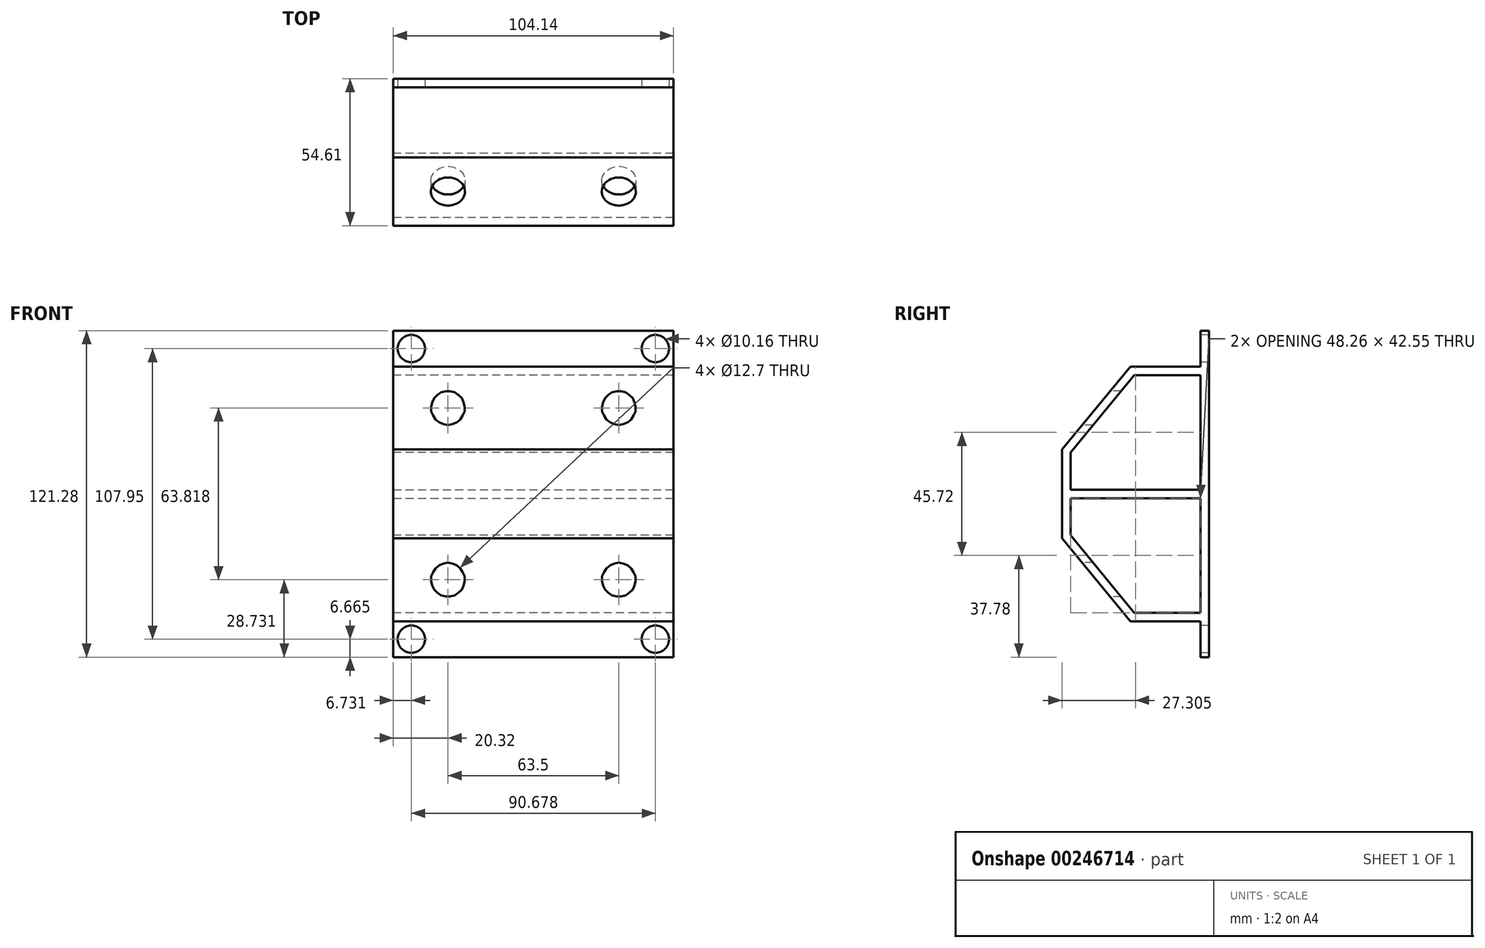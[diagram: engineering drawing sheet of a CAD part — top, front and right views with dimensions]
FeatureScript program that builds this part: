
annotation { "Feature Type Name" : "Feature", "Feature Type Description" : "" }
export const myFeature = defineFeature(function(context is Context, id is Id, definition is map)
    precondition{}
    {
        {
            var Q0;
            Q0=qCreatedBy(makeId("Right.planeOp"),FACE);
            var sketch = newSketch(context, id + "F0", { "sketchPlane" : qUnion([Q0])});
            skLineSegment(sketch, "E0", {"start": v(0, 0) * mm, "end": v(57.67, 0) * mm, "construction": true});
            skLineSegment(sketch, "E1", {"start": v(29.21, 47.3) * mm, "end": v(0, 47.3) * mm});
            skLineSegment(sketch, "E2", {"start": v(0, 47.3) * mm, "end": v(-25.4, 16.51) * mm});
            skLineSegment(sketch, "E3", {"start": v(-25.4, 16.51) * mm, "end": v(-25.4, 0) * mm});
            skLineSegment(sketch, "E4", {"start": v(0, 0) * mm, "end": v(0, 100.35) * mm, "construction": true});
            skLineSegment(sketch, "E5", {"start": v(29.21, 47.3) * mm, "end": v(29.21, 0) * mm});
            skLineSegment(sketch, "E6.MirrorCS", {"start": v(29.21, -47.3) * mm, "end": v(29.21, 0) * mm});
            skLineSegment(sketch, "E7.MirrorCS", {"start": v(0, -47.3) * mm, "end": v(-25.4, -16.51) * mm});
            skLineSegment(sketch, "E8.MirrorCS", {"start": v(-25.4, -16.51) * mm, "end": v(-25.4, 0) * mm});
            skLineSegment(sketch, "E9.MirrorCS", {"start": v(29.21, -47.3) * mm, "end": v(0, -47.3) * mm});
            skLineSegment(sketch, "E10", {"start": v(-22.22, 3.17) * mm, "end": v(26.04, 3.17) * mm});
            skLineSegment(sketch, "E11.MirrorCS", {"start": v(-22.22, -3.17) * mm, "end": v(26.04, -3.17) * mm});
            skLineSegment(sketch, "E12.0", {"start": v(26.04, 44.13) * mm, "end": v(1.5, 44.13) * mm});
            skLineSegment(sketch, "E12.1", {"start": v(26.03, 44.13) * mm, "end": v(26.04, 0) * mm});
            skLineSegment(sketch, "E12.2", {"start": v(1.5, 44.13) * mm, "end": v(-22.22, 15.37) * mm});
            skLineSegment(sketch, "E12.3", {"start": v(26.04, -44.13) * mm, "end": v(26.03, 0) * mm});
            skLineSegment(sketch, "E12.4", {"start": v(-22.22, 15.37) * mm, "end": v(-22.22, 0) * mm});
            skLineSegment(sketch, "E12.5", {"start": v(-22.22, -15.37) * mm, "end": v(-22.22, 0) * mm});
            skLineSegment(sketch, "E12.6", {"start": v(1.5, -44.13) * mm, "end": v(-22.23, -15.37) * mm});
            skLineSegment(sketch, "E12.7", {"start": v(26.04, -44.13) * mm, "end": v(1.5, -44.13) * mm});
            skPoint(sketch, "E13.orphan", {"position": v(-25.4, 3.17) * mm});
            skPoint(sketch, "E14.orphan", {"position": v(-25.4, -3.17) * mm});
            skPoint(sketch, "E15.orphan", {"position": v(29.21, 3.18) * mm});
            skPoint(sketch, "E16.orphan", {"position": v(29.21, -3.18) * mm});
            skLineSegment(sketch, "E17", {"start": v(-22.22, 3.17) * mm, "end": v(-22.22, -3.17) * mm});
            skLineSegment(sketch, "E18", {"start": v(26.04, 3.18) * mm, "end": v(26.04, -3.18) * mm});
            skSolve(sketch);
        }
        {
            var Q0;
            Q0 = qSketchRegion(id + "F0", true);
            extrude(context, id + "F1", {"entities" : qUnion([Q0]), "depth" : 52.07 * mm, "hasSecondDirection" : true, "secondDirectionOppositeDirection" : true, "secondDirectionDepth" : 52.07 * mm});
        }
        {
            var Q0;
            Q0=makeQuery(id+"F1.opExtrude","CAP_FACE",FACE,{"disambiguationData":[OSD([sQuery(id+"F0.wireOp",EDGE,"E1"),sQuery(id+"F0.wireOp",EDGE,"E2"),sQuery(id+"F0.wireOp",EDGE,"E3"),sQuery(id+"F0.wireOp",EDGE,"E5"),sQuery(id+"F0.wireOp",EDGE,"E6.MirrorCS"),sQuery(id+"F0.wireOp",EDGE,"E7.MirrorCS"),sQuery(id+"F0.wireOp",EDGE,"E8.MirrorCS"),sQuery(id+"F0.wireOp",EDGE,"E9.MirrorCS"),sQuery(id+"F0.wireOp",EDGE,"E12.0"),sQuery(id+"F0.wireOp",EDGE,"E12.1"),sQuery(id+"F0.wireOp",EDGE,"E12.2"),sQuery(id+"F0.wireOp",EDGE,"E12.3"),sQuery(id+"F0.wireOp",EDGE,"E12.4"),sQuery(id+"F0.wireOp",EDGE,"E12.5"),sQuery(id+"F0.wireOp",EDGE,"E12.6"),sQuery(id+"F0.wireOp",EDGE,"E12.7"),sQuery(id+"F0.wireOp",EDGE,"E17"),sQuery(id+"F0.wireOp",EDGE,"E18")])],"isStart":false});
            var sketch = newSketch(context, id + "F2", { "sketchPlane" : qUnion([Q0])});
            skLineSegment(sketch, "E19", {"start": v(-22.22, 1.59) * mm, "end": v(26.04, 1.59) * mm});
            skLineSegment(sketch, "E20", {"start": v(0, 0) * mm, "end": v(9.33, 0) * mm, "construction": true});
            skLineSegment(sketch, "E21.MirrorCS", {"start": v(-22.22, -1.59) * mm, "end": v(26.04, -1.59) * mm});
            skLineSegment(sketch, "E22", {"start": v(-22.22, 1.59) * mm, "end": v(-22.22, -1.59) * mm});
            skLineSegment(sketch, "E23", {"start": v(26.04, 1.59) * mm, "end": v(26.04, -1.59) * mm});
            skSolve(sketch);
        }
        {
            var Q0;
            Q0 = qSketchRegion(id + "F2", true);
            var Q1;
            Q1=makeQuery(id+"F1.opExtrude","CAP_FACE",FACE,{"disambiguationData":[OSD([sQuery(id+"F0.wireOp",EDGE,"E1"),sQuery(id+"F0.wireOp",EDGE,"E2"),sQuery(id+"F0.wireOp",EDGE,"E3"),sQuery(id+"F0.wireOp",EDGE,"E5"),sQuery(id+"F0.wireOp",EDGE,"E6.MirrorCS"),sQuery(id+"F0.wireOp",EDGE,"E7.MirrorCS"),sQuery(id+"F0.wireOp",EDGE,"E8.MirrorCS"),sQuery(id+"F0.wireOp",EDGE,"E9.MirrorCS"),sQuery(id+"F0.wireOp",EDGE,"E12.0"),sQuery(id+"F0.wireOp",EDGE,"E12.1"),sQuery(id+"F0.wireOp",EDGE,"E12.2"),sQuery(id+"F0.wireOp",EDGE,"E12.3"),sQuery(id+"F0.wireOp",EDGE,"E12.4"),sQuery(id+"F0.wireOp",EDGE,"E12.5"),sQuery(id+"F0.wireOp",EDGE,"E12.6"),sQuery(id+"F0.wireOp",EDGE,"E12.7"),sQuery(id+"F0.wireOp",EDGE,"E17"),sQuery(id+"F0.wireOp",EDGE,"E18")])],"isStart":true});
            extrude(context, id + "F3", {"entities" : qUnion([Q0]), "operationType" : NewBodyOperationType.ADD, "endBound" : BoundingType.UP_TO_SURFACE, "oppositeDirection" : true, "endBoundEntityFace" : qUnion([Q1]), "depth" : 25.4 * mm});
        }
        {
            var Q0;
            Q0=makeQuery(id+"F1.opExtrude","SWEPT_FACE",FACE,{"disambiguationData":[OSD([sQuery(id+"F0.wireOp",EDGE,"E5"),sQuery(id+"F0.wireOp",EDGE,"E6.MirrorCS")])]});
            var sketch = newSketch(context, id + "F4", { "sketchPlane" : qUnion([Q0])});
            skLineSegment(sketch, "E24", {"start": v(-52.07, 47.3) * mm, "end": v(-52.07, 60.64) * mm});
            skLineSegment(sketch, "E25", {"start": v(-52.07, 60.64) * mm, "end": v(52.07, 60.64) * mm});
            skLineSegment(sketch, "E26", {"start": v(52.07, 60.64) * mm, "end": v(52.07, 47.3) * mm});
            skLineSegment(sketch, "E27", {"start": v(52.07, 47.3) * mm, "end": v(-52.07, 47.3) * mm});
            skLineSegment(sketch, "E28", {"start": v(0, 0) * mm, "end": v(26.61, 0) * mm, "construction": true});
            skLineSegment(sketch, "E29.MirrorCS", {"start": v(52.07, -47.3) * mm, "end": v(-52.07, -47.3) * mm});
            skLineSegment(sketch, "E30.MirrorCS", {"start": v(52.07, -60.64) * mm, "end": v(52.07, -47.3) * mm});
            skLineSegment(sketch, "E31.MirrorCS", {"start": v(-52.07, -60.64) * mm, "end": v(52.07, -60.64) * mm});
            skLineSegment(sketch, "E32.MirrorCS", {"start": v(-52.07, -47.3) * mm, "end": v(-52.07, -60.64) * mm});
            skSolve(sketch);
        }
        {
            var Q0;
            Q0 = qSketchRegion(id + "F4", true);
            extrude(context, id + "F5", {"entities" : qUnion([Q0]), "operationType" : NewBodyOperationType.ADD, "oppositeDirection" : true, "depth" : 3.17 * mm});
        }
        {
            var Q0;
            Q0=makeQuery(id+"F5.opExtrude","CAP_FACE",FACE,{"disambiguationData":[OSD([sQuery(id+"F4.wireOp",EDGE,"E24"),sQuery(id+"F4.wireOp",EDGE,"E25"),sQuery(id+"F4.wireOp",EDGE,"E26"),sQuery(id+"F4.wireOp",EDGE,"E27")])],"isStart":false});
            var sketch = newSketch(context, id + "F6", { "sketchPlane" : qUnion([Q0])});
            skCircle(sketch, "E33", {"center": v(-45.34, 53.97) * mm, "radius": 5.08 * mm});
            skPoint(sketch, "E33.centerSnap0", {"position": v(-52.07, 53.97) * mm});
            skCircle(sketch, "E34", {"center": v(45.34, 53.97) * mm, "radius": 5.08 * mm});
            skLineSegment(sketch, "E35", {"start": v(0, 0) * mm, "end": v(81.74, 0) * mm, "construction": true});
            skCircle(sketch, "E36.MirrorC", {"center": v(45.34, -53.97) * mm, "radius": 5.08 * mm});
            skCircle(sketch, "E37.MirrorC", {"center": v(-45.34, -53.98) * mm, "radius": 5.08 * mm});
            skSolve(sketch);
        }
        {
            var Q0;
            Q0 = qSketchRegion(id + "F6", true);
            var Q1;
            Q1=makeQuery(id+"F5.boolean.opBoolean","MERGE",FACE,{"derivedFrom":[makeQuery(id+"F1.opExtrude","SWEPT_FACE",FACE,{"disambiguationData":[OSD([sQuery(id+"F0.wireOp",EDGE,"E5"),sQuery(id+"F0.wireOp",EDGE,"E6.MirrorCS")])]}),makeQuery(id+"F5.opExtrude","CAP_FACE",FACE,{"disambiguationData":[OSD([sQuery(id+"F4.wireOp",EDGE,"E24"),sQuery(id+"F4.wireOp",EDGE,"E25"),sQuery(id+"F4.wireOp",EDGE,"E26"),sQuery(id+"F4.wireOp",EDGE,"E27")])],"isStart":true}),makeQuery(id+"F5.opExtrude","CAP_FACE",FACE,{"disambiguationData":[OSD([sQuery(id+"F4.wireOp",EDGE,"E29.MirrorCS"),sQuery(id+"F4.wireOp",EDGE,"E30.MirrorCS"),sQuery(id+"F4.wireOp",EDGE,"E31.MirrorCS"),sQuery(id+"F4.wireOp",EDGE,"E32.MirrorCS")])],"isStart":true})]});
            extrude(context, id + "F7", {"entities" : qUnion([Q0]), "operationType" : NewBodyOperationType.REMOVE, "endBound" : BoundingType.UP_TO_SURFACE, "oppositeDirection" : true, "endBoundEntityFace" : qUnion([Q1]), "depth" : 25.4 * mm});
        }
        {
            var Q0;
            Q0=makeQuery(id+"F1.opExtrude","SWEPT_FACE",FACE,{"disambiguationData":[OSD([sQuery(id+"F0.wireOp",EDGE,"E3"),sQuery(id+"F0.wireOp",EDGE,"E8.MirrorCS")])]});
            var sketch = newSketch(context, id + "F8", { "sketchPlane" : qUnion([Q0])});
            skCircle(sketch, "E38", {"center": v(-31.75, 31.9) * mm, "radius": 6.35 * mm});
            skLineSegment(sketch, "E39", {"start": v(0, 0) * mm, "end": v(0, 55.11) * mm, "construction": true});
            skLineSegment(sketch, "E40", {"start": v(0, 0) * mm, "end": v(34.58, 0) * mm, "construction": true});
            skLineSegment(sketch, "E41", {"start": v(52.07, 47.3) * mm, "end": v(52.07, 16.5) * mm, "construction": true});
            skLineSegment(sketch, "E42", {"start": v(52.07, 31.9) * mm, "end": v(-54.5, 31.9) * mm, "construction": true});
            skCircle(sketch, "E43.MirrorC", {"center": v(31.75, 31.9) * mm, "radius": 6.35 * mm});
            skCircle(sketch, "E44.MirrorC", {"center": v(31.75, -31.9) * mm, "radius": 6.35 * mm});
            skCircle(sketch, "E45.MirrorC", {"center": v(-31.75, -31.9) * mm, "radius": 6.35 * mm});
            skSolve(sketch);
        }
        {
            var Q0;
            Q0 = qSketchRegion(id + "F8", true);
            var Q1;
            {var subQ0=sQuery(id+"F0.wireOp",EDGE,"E18");var subQ6=sQuery(id+"F0.wireOp",EDGE,"E12.3");var subQ8=sQuery(id+"F0.wireOp",EDGE,"E12.1");var subQ9=sQuery(id+"F0.wireOp",EDGE,"E12.0");Q1=makeQuery(id+"F3.boolean.opBoolean","SPLIT",FACE,{"disambiguationData":[TD([makeQuery(id+"F1.opExtrude","SWEPT_FACE",FACE,{"disambiguationData":[OSD([subQ9])]})])],"derivedFrom":makeQuery(id+"F1.opExtrude","SWEPT_FACE",FACE,{"disambiguationData":[OSD([subQ8,subQ6,subQ0])]})});}
            extrude(context, id + "F9", {"entities" : qUnion([Q0]), "operationType" : NewBodyOperationType.REMOVE, "endBound" : BoundingType.UP_TO_SURFACE, "oppositeDirection" : true, "endBoundEntityFace" : qUnion([Q1]), "depth" : 25.4 * mm});
        }
    });
